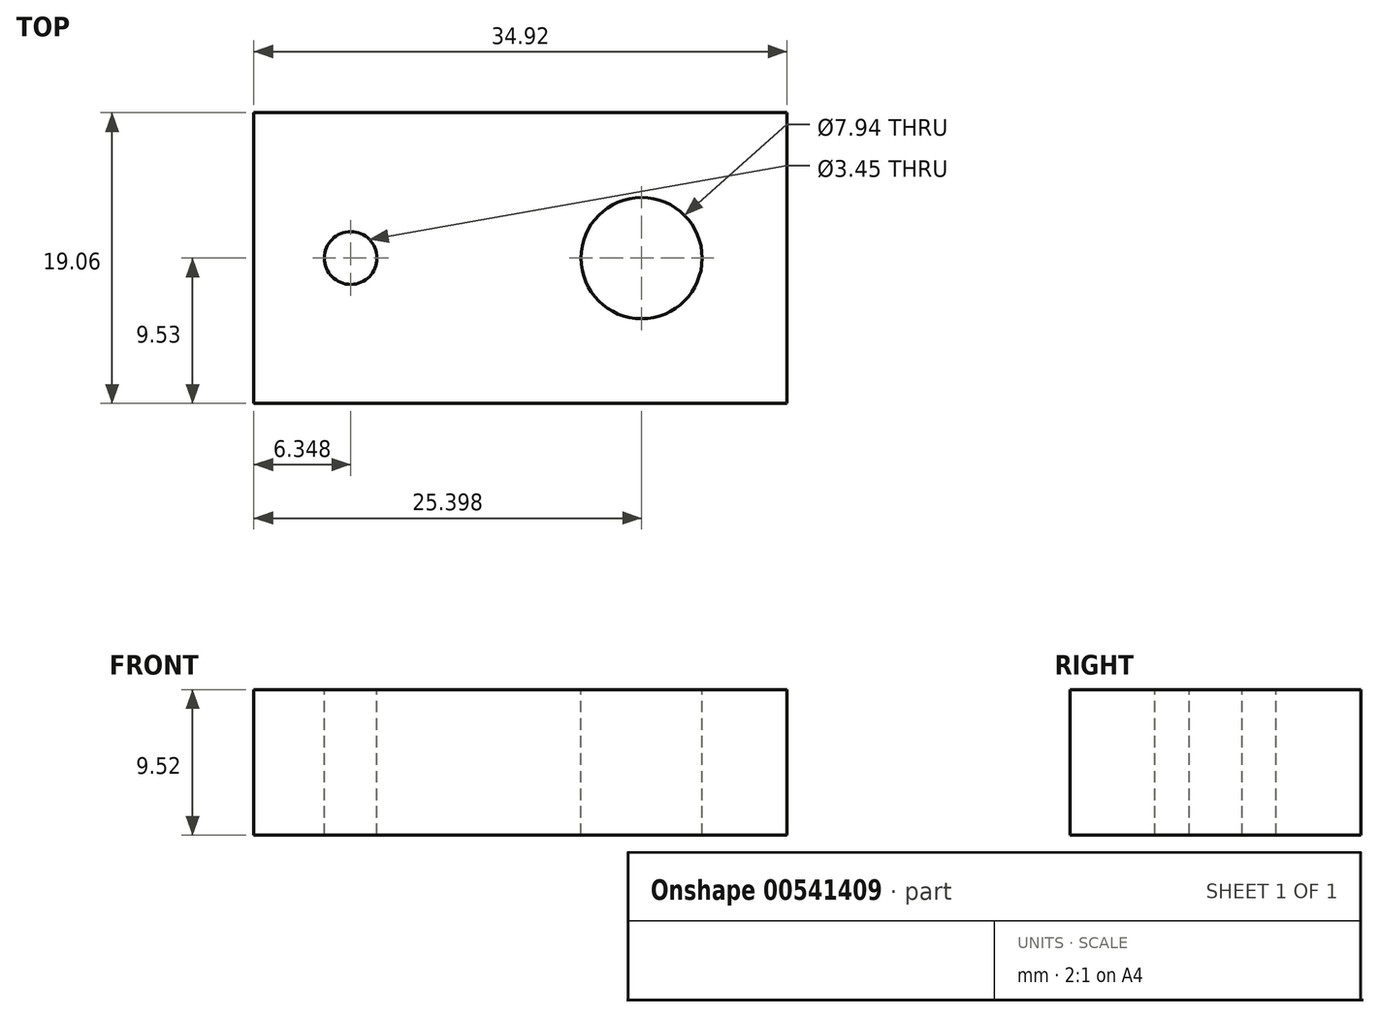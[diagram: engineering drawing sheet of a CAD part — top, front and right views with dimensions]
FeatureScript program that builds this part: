
annotation { "Feature Type Name" : "Feature", "Feature Type Description" : "" }
export const myFeature = defineFeature(function(context is Context, id is Id, definition is map)
    precondition{}
    {
        {
            var Q0;
            Q0=qCreatedBy(makeId("Right.planeOp"),FACE);
            var sketch = newSketch(context, id + "F0", { "sketchPlane" : qUnion([Q0])});
            skLineSegment(sketch, "E0.bottom", {"start": v(9.53, 4.76) * mm, "end": v(-9.53, 4.76) * mm});
            skLineSegment(sketch, "E0.top", {"start": v(9.53, -4.76) * mm, "end": v(-9.53, -4.76) * mm});
            skLineSegment(sketch, "E0.left", {"start": v(9.53, 4.76) * mm, "end": v(9.53, -4.76) * mm});
            skLineSegment(sketch, "E0.right", {"start": v(-9.53, 4.76) * mm, "end": v(-9.53, -4.76) * mm});
            skPoint(sketch, "E0.middle", {"position": v(0, 0) * mm});
            skSolve(sketch);
        }
        {
            var Q0;
            Q0=makeQuery(id+"F0.imprint","IMPRINT",FACE,{"disambiguationData":[TD([[makeQuery(id+"F0.imprint","IMPRINT",EDGE,{"derivedFrom":sQuery(id+"F0.wireOp",EDGE,"E0.bottom")}),1.0]])]});
            extrude(context, id + "F1", {"entities" : qUnion([Q0]), "endBound" : BoundingType.SYMMETRIC, "depth" : 34.92 * mm, "offsetDistance" : 25.4 * mm});
        }
        {
            var Q0;
            Q0=makeQuery(id+"F1.opExtrude","SWEPT_FACE",FACE,{"disambiguationData":[OSD([sQuery(id+"F0.wireOp",EDGE,"E0.bottom")])]});
            var sketch = newSketch(context, id + "F2", { "sketchPlane" : qUnion([Q0])});
            skPoint(sketch, "E1", {"position": v(7.94, 0) * mm});
            skSolve(sketch);
        }
        {
            var Q0;
            Q0=sQuery(id+"F2.wireOp",VERTEX,"E1");
            var Q1;
            Q1=makeQuery(id+"F1.opExtrude","SWEPT_BODY",BODY,{"disambiguationData":[OSD([sQuery(id+"F0.wireOp",EDGE,"E0.bottom"),sQuery(id+"F0.wireOp",EDGE,"E0.top"),sQuery(id+"F0.wireOp",EDGE,"E0.left"),sQuery(id+"F0.wireOp",EDGE,"E0.right")])]});
            hole(context, id + "F3", {"style" : HoleStyle.SIMPLE, "endStyle" : HoleEndStyle.THROUGH, "standardTappedOrClearance" : lookupTablePath({ "standard" : "ANSI", "fit" : "Normal (ASME)", "engagement" : "75%", "pitch" : "16 tpi", "size" : "3/8", "type" : "Tapped" }), "standardBlindInLast" : lookupTablePath({ "fit" : "Free", "standard" : "ANSI", "engagement" : "75%", "pitch" : "16 tpi", "size" : "3/8", "type" : "Tapped" }), "holeDiameter" : 7.94 * mm, "showTappedDepth" : true, "isTappedThrough" : true, "tappedDepth" : 12.7 * mm, "tapClearance" : 3, "locations" : qUnion([Q0]), "scope" : qUnion([Q1]), "majorDiameter" : 9.53 * mm});
        }
        {
            var Q0;
            Q0=makeQuery(id+"F1.opExtrude","SWEPT_FACE",FACE,{"disambiguationData":[OSD([sQuery(id+"F0.wireOp",EDGE,"E0.bottom")])]});
            var sketch = newSketch(context, id + "F4", { "sketchPlane" : qUnion([Q0])});
            skPoint(sketch, "E2", {"position": v(-11.11, 0) * mm});
            skSolve(sketch);
        }
        {
            var Q0;
            Q0=sQuery(id+"F4.wireOp",VERTEX,"E2");
            var Q1;
            Q1=makeQuery(id+"F1.opExtrude","SWEPT_BODY",BODY,{"disambiguationData":[OSD([sQuery(id+"F0.wireOp",EDGE,"E0.bottom"),sQuery(id+"F0.wireOp",EDGE,"E0.top"),sQuery(id+"F0.wireOp",EDGE,"E0.left"),sQuery(id+"F0.wireOp",EDGE,"E0.right")])]});
            hole(context, id + "F5", {"style" : HoleStyle.SIMPLE, "endStyle" : HoleEndStyle.THROUGH, "standardTappedOrClearance" : lookupTablePath({ "standard" : "ANSI", "fit" : "Normal (ASME)", "engagement" : "75%", "pitch" : "32 tpi", "size" : "#8", "type" : "Tapped" }), "standardBlindInLast" : lookupTablePath({ "fit" : "Free", "standard" : "ANSI", "engagement" : "75%", "pitch" : "32 tpi", "size" : "#8", "type" : "Tapped" }), "holeDiameter" : 3.45 * mm, "showTappedDepth" : true, "isTappedThrough" : true, "tappedDepth" : 12.7 * mm, "tapClearance" : 3, "locations" : qUnion([Q0]), "scope" : qUnion([Q1]), "majorDiameter" : 4.17 * mm});
        }
    });
